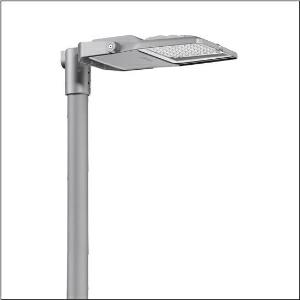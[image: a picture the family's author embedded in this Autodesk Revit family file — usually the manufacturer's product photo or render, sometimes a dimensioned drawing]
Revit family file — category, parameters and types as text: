
# Revit family: floodlight_fl_21_iq_mini___pl43_5xa7771c4a3a_be4f
name_source: partatom
category: Lighting Fixtures
units: mm (PartAtom-declared; Revit-internal decimal feet)

## family parameters
Cut with Voids When Loaded = No
Host = Face
Light Source = No
Part Type = Normal
Room Calculation Point = No
Round Connector Dimension = Use Diameter
Shared = No

## types (1)
- --- (1 x LED, 13050 lm, 87.2 W, 4000K)
    Apparent Load = 87 VA
    CIE Flux Codes = 27 78 99 100 100
    Color Rendering = 70
    Color Temperature = 4000K
    Default Elevation = 1800 mm
    Description = Floodlight FL 21 iQ mini, floodlight, primary light control with lens, of PMMA, primary optical cover: protective disc, of toughened safety glass, transparent, light distribution: PL43, light emission: direct distribution, installation type: surface-mounted, LED, High Power LED, rated luminous flux: 13.050lm, luminous efficacy: 150lm/W, light colour: 740, colour temperature: 4000K, control: Auto-Match, Temp-Guard, Lumen-Switch, Night-Set, Smart-Wire, Light-Fading, Desk-Remote (wireless, voltage-free reading and setting of iQ features in the workshop via application-optimized NFC function/RFID function), optimised constant luminous flux control (CLO 2.0), with terminal, 6-pole, mains connection: 220..240V, AC, 50/60Hz, start of lifetime: 87W, end of service life: 92W, reduction: 40W, luminaire housing, of diecast aluminium, powder-coated, Siteco® metallic grey (DB 702S), corrosivity category C5 mid according to DIN EN ISO 12944, sealing non-destructively replaceable, please order mast flange separately, mast bracket, of steel, galvanised, powder-coated, Siteco® metallic grey (DB 702S), protection rating (complete): IP66, insulation class (complete): insulation class II (safety insulation), certification: CE, ENEC, VDE, protection symbol: D, impact resistance: IK08, permissible operating ambient temperature: -40..+40°C, permissible operating ambient temperature for outdoor applications: -40..+50°C, standard: DIN EN 12944, LABS conformity tested according to VDMA 24364:2018-05, packaging unit: 1 piece

Light Distribution: PL43
    Height = 70 mm
    Lamp = 1 x LED
    Lamp Light Flux = 13050 lm
    Lamp Power = 87.2 W
    Lamp count = 1
    Length = 485 mm
    Luminous efficacy = 150 lm/W
    Manufacturer = Siteco
    ModVariant = No
    Model = 5XA7771C4A3A
    Number of Poles = 1
    OnlyDefault = Yes
    Power Factor = 1
    Product Name = Floodlight FL 21 iQ mini | PL43
    Product group = floodlight | pylon annexe
    ProductGroupID = 6200
    Protection Class = Protection class II
    Protection Degree = IP 66
    RLX_Detail_Level = 1
    RLX_Emergency_Light_Flux = 0 lm
    RLX_Emergency_Type = 0
    RLX_Emergency_Type_DB = No
    RlxData = <blob elided: 101269 chars, md5=df9417e7>
    Socket = socket
    Standby Power = 0 W
    System Light Flux = 13050 lm
    System Power = 87 W
    Type Comments = factory setting: luminous flux: 100 % | dim-lin: 254 | 456 mA
    Type Image = l_1007125.jpg
    URL = http://relux.com
    VarID = @adj_094729
    Voltage = 0 V
    Weight = 0.00 kg
    Width = 337 mm

## geometry (parser evidence)
native form markers: Blend x4, Sweep x12
no freeform markers — native parametric forms only
